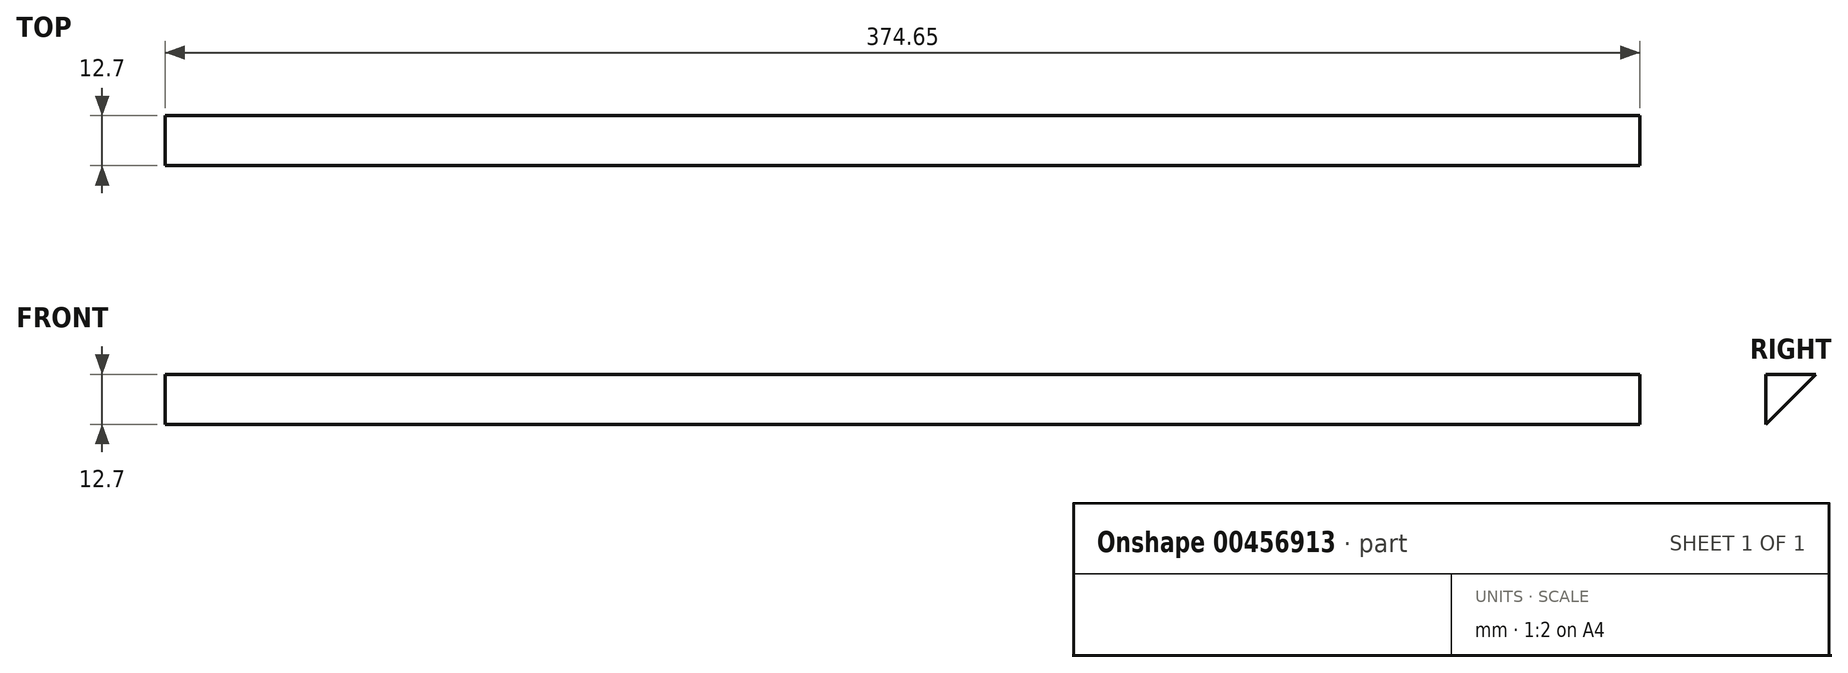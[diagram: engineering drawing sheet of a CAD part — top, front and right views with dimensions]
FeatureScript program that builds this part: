
annotation { "Feature Type Name" : "Feature", "Feature Type Description" : "" }
export const myFeature = defineFeature(function(context is Context, id is Id, definition is map)
    precondition{}
    {
        {
            var Q0;
            Q0=qCreatedBy(makeId("Right.planeOp"),FACE);
            var sketch = newSketch(context, id + "F0", { "sketchPlane" : qUnion([Q0])});
            skLineSegment(sketch, "E0.bottom", {"start": v(-7.86, -11.64) * mm, "end": v(4.84, -11.64) * mm});
            skLineSegment(sketch, "E0.left", {"start": v(-7.86, -11.64) * mm, "end": v(-7.86, -24.34) * mm});
            skLineSegment(sketch, "E0.right", {"start": v(4.84, -11.64) * mm, "end": v(4.84, -11.64) * mm});
            skLineSegment(sketch, "E1", {"start": v(-7.86, -24.34) * mm, "end": v(4.84, -11.64) * mm});
            skSolve(sketch);
        }
        {
            var Q0;
            Q0=makeQuery(id+"F0.imprint","IMPRINT",FACE,{"disambiguationData":[TD([[makeQuery(id+"F0.imprint","IMPRINT",EDGE,{"derivedFrom":sQuery(id+"F0.wireOp",EDGE,"E0.bottom")}),-1.0]])]});
            extrude(context, id + "F1", {"entities" : qUnion([Q0]), "depth" : 374.65 * mm});
        }
    });
